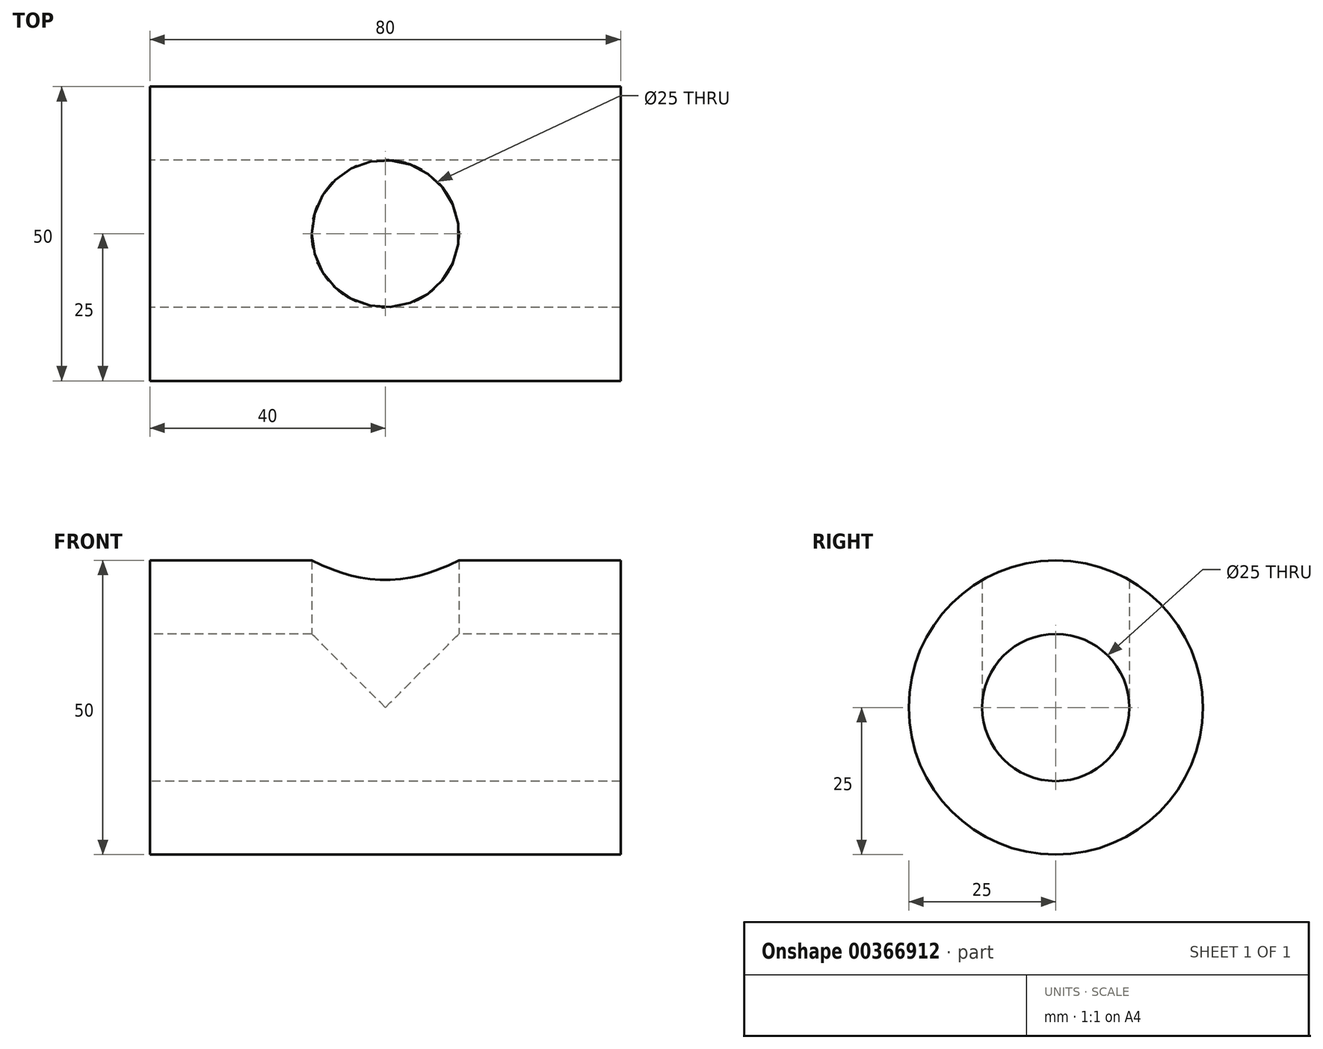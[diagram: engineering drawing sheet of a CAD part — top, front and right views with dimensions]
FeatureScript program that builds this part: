
annotation { "Feature Type Name" : "Feature", "Feature Type Description" : "" }
export const myFeature = defineFeature(function(context is Context, id is Id, definition is map)
    precondition{}
    {
        {
            var Q0;
            Q0=qCreatedBy(makeId("Right.planeOp"),FACE);
            var sketch = newSketch(context, id + "F0", { "sketchPlane" : qUnion([Q0])});
            skCircle(sketch, "E0", {"center": v(0, 0) * mm, "radius": 25 * mm});
            skSolve(sketch);
        }
        {
            var Q0;
            Q0 = qSketchRegion(id + "F0", true);
            extrude(context, id + "F1", {"entities" : qUnion([Q0]), "endBound" : BoundingType.SYMMETRIC, "depth" : 80 * mm});
        }
        {
            var Q0;
            Q0=qCreatedBy(makeId("Top.planeOp"),FACE);
            var sketch = newSketch(context, id + "F2", { "sketchPlane" : qUnion([Q0])});
            skCircle(sketch, "E1", {"center": v(0, 0) * mm, "radius": 12.5 * mm});
            skSolve(sketch);
        }
        {
            var Q0;
            Q0 = qSketchRegion(id + "F2", true);
            extrude(context, id + "F3", {"entities" : qUnion([Q0]), "operationType" : NewBodyOperationType.REMOVE, "depth" : 25 * mm});
        }
        {
            var Q0;
            Q0=qCreatedBy(makeId("Right.planeOp"),FACE);
            var sketch = newSketch(context, id + "F4", { "sketchPlane" : qUnion([Q0])});
            skCircle(sketch, "E2", {"center": v(0, 0) * mm, "radius": 12.5 * mm});
            skSolve(sketch);
        }
        {
            var Q0;
            Q0 = qSketchRegion(id + "F4", true);
            extrude(context, id + "F5", {"entities" : qUnion([Q0]), "operationType" : NewBodyOperationType.REMOVE, "endBound" : BoundingType.THROUGH_ALL, "depth" : 25 * mm, "hasSecondDirection" : true, "secondDirectionBound" : SecondDirectionBoundingType.THROUGH_ALL, "secondDirectionOppositeDirection" : true, "secondDirectionDepth" : 25 * mm});
        }
    });
